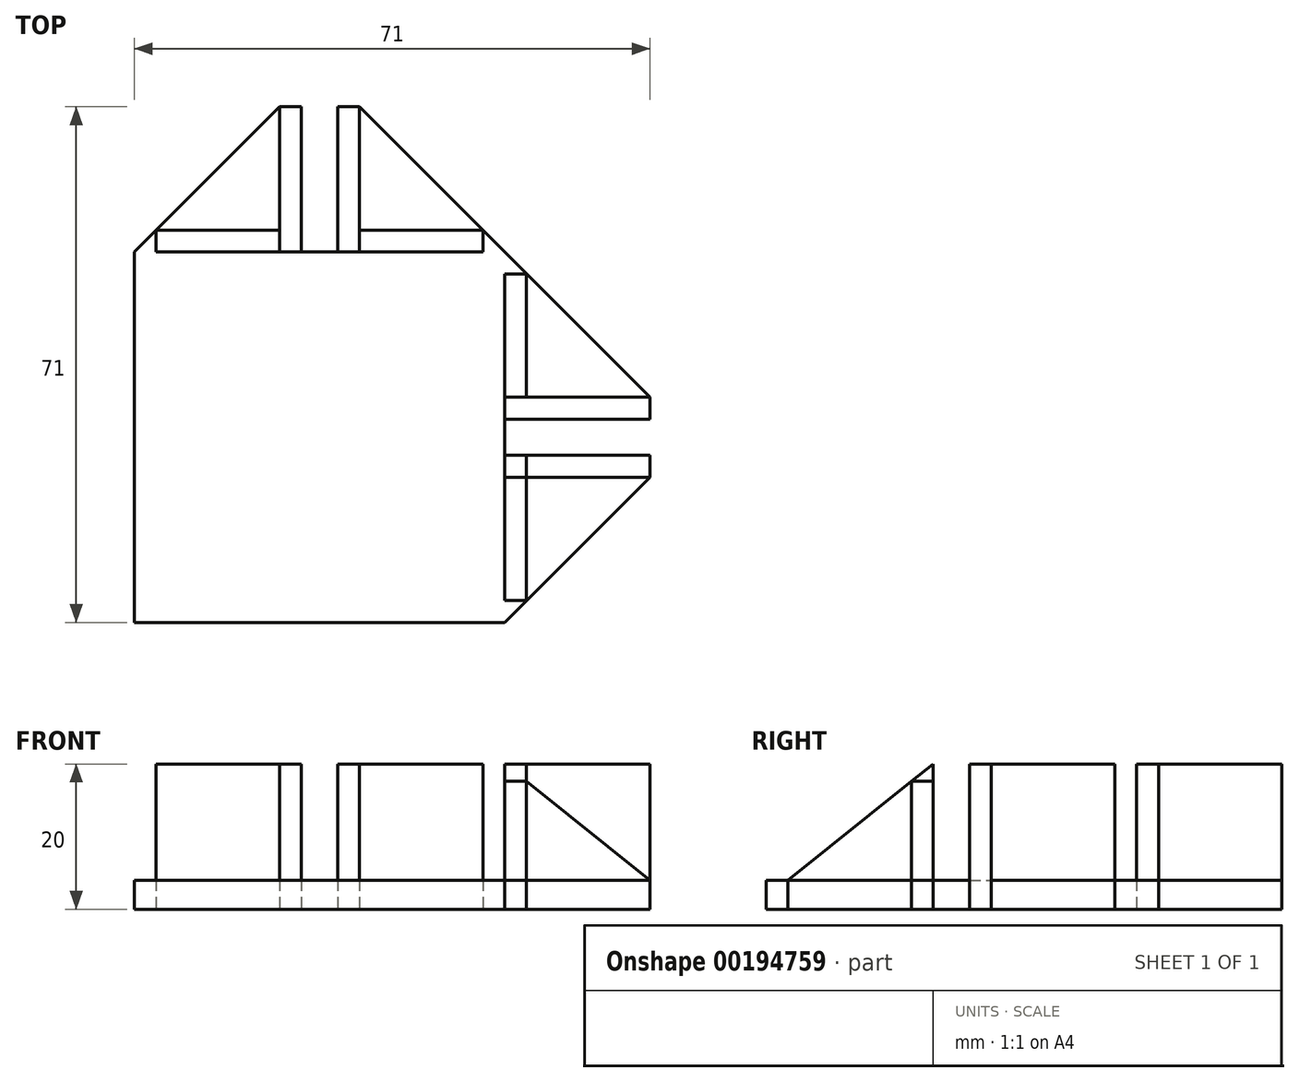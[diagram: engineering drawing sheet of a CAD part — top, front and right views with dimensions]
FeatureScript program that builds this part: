
annotation { "Feature Type Name" : "Feature", "Feature Type Description" : "" }
export const myFeature = defineFeature(function(context is Context, id is Id, definition is map)
    precondition{}
    {
        {
            var Q0;
            Q0=qCreatedBy(makeId("Top.planeOp"),FACE);
            var sketch = newSketch(context, id + "F0", { "sketchPlane" : qUnion([Q0])});
            skLineSegment(sketch, "E0.bottom", {"start": v(25.5, -25.5) * mm, "end": v(-25.5, -25.5) * mm});
            skLineSegment(sketch, "E0.top", {"start": v(25.5, 25.5) * mm, "end": v(-25.5, 25.5) * mm});
            skLineSegment(sketch, "E0.left", {"start": v(25.5, -25.5) * mm, "end": v(25.5, 25.5) * mm});
            skLineSegment(sketch, "E0.right", {"start": v(-25.5, -25.5) * mm, "end": v(-25.5, 25.5) * mm});
            skPoint(sketch, "E0.middle", {"position": v(0, 0) * mm});
            skLineSegment(sketch, "E1", {"start": v(-25.5, 25.5) * mm, "end": v(-5.5, 25.5) * mm});
            skLineSegment(sketch, "E2", {"start": v(-5.5, 25.5) * mm, "end": v(-5.5, 45.5) * mm});
            skLineSegment(sketch, "E3", {"start": v(-5.5, 45.5) * mm, "end": v(-25.5, 25.5) * mm});
            skLineSegment(sketch, "E4.MirrorCS", {"start": v(25.5, 25.5) * mm, "end": v(5.5, 25.5) * mm});
            skLineSegment(sketch, "E5.MirrorCS", {"start": v(5.5, 45.5) * mm, "end": v(25.5, 25.5) * mm});
            skLineSegment(sketch, "E6.MirrorCS", {"start": v(5.5, 25.5) * mm, "end": v(5.5, 45.5) * mm});
            skLineSegment(sketch, "E7", {"start": v(25.5, -25.5) * mm, "end": v(25.5, -5.5) * mm});
            skLineSegment(sketch, "E8", {"start": v(25.5, -5.5) * mm, "end": v(45.5, -5.5) * mm});
            skLineSegment(sketch, "E9", {"start": v(45.5, -5.5) * mm, "end": v(25.5, -25.5) * mm});
            skLineSegment(sketch, "E10.MirrorCS", {"start": v(45.5, 5.5) * mm, "end": v(25.5, 25.5) * mm});
            skLineSegment(sketch, "E11.MirrorCS", {"start": v(25.5, 5.5) * mm, "end": v(45.5, 5.5) * mm});
            skLineSegment(sketch, "E12.MirrorCS", {"start": v(25.5, 25.5) * mm, "end": v(25.5, 5.5) * mm});
            skSolve(sketch);
        }
        {
            var Q0;
            Q0 = qSketchRegion(id + "F0", true);
            extrude(context, id + "F1", {"entities" : qUnion([Q0]), "depth" : 4 * mm});
        }
        {
            var Q0;
            Q0=qCreatedBy(makeId("Top.planeOp"),FACE);
            var sketch = newSketch(context, id + "F2", { "sketchPlane" : qUnion([Q0])});
            skLineSegment(sketch, "E13.0", {"start": v(-5.5, 25.5) * mm, "end": v(-5.5, 45.5) * mm});
            skLineSegment(sketch, "E13.1", {"start": v(5.5, 25.5) * mm, "end": v(-5.5, 25.5) * mm});
            skLineSegment(sketch, "E13.2", {"start": v(5.5, 25.5) * mm, "end": v(5.5, 45.5) * mm});
            skLineSegment(sketch, "E13.3", {"start": v(25.5, 5.5) * mm, "end": v(45.5, 5.5) * mm});
            skLineSegment(sketch, "E13.4", {"start": v(25.5, -5.5) * mm, "end": v(45.5, -5.5) * mm});
            skLineSegment(sketch, "E13.5", {"start": v(25.5, -5.5) * mm, "end": v(25.5, 5.5) * mm});
            skLineSegment(sketch, "E14", {"start": v(-5.5, 45.5) * mm, "end": v(-2.5, 45.5) * mm});
            skLineSegment(sketch, "E15", {"start": v(-2.5, 45.5) * mm, "end": v(-2.5, 25.5) * mm});
            skLineSegment(sketch, "E16.MirrorCS", {"start": v(5.5, 45.5) * mm, "end": v(2.5, 45.5) * mm});
            skLineSegment(sketch, "E17.MirrorCS", {"start": v(2.5, 45.5) * mm, "end": v(2.5, 25.5) * mm});
            skLineSegment(sketch, "E18", {"start": v(45.5, 5.5) * mm, "end": v(45.5, 2.5) * mm});
            skLineSegment(sketch, "E19", {"start": v(45.5, 2.5) * mm, "end": v(25.5, 2.5) * mm});
            skLineSegment(sketch, "E20.MirrorCS", {"start": v(45.5, -2.5) * mm, "end": v(25.5, -2.5) * mm});
            skLineSegment(sketch, "E21.MirrorCS", {"start": v(45.5, -5.5) * mm, "end": v(45.5, -2.5) * mm});
            skLineSegment(sketch, "E22", {"start": v(25.5, -2.5) * mm, "end": v(25.5, -22.5) * mm});
            skLineSegment(sketch, "E23", {"start": v(25.5, -22.5) * mm, "end": v(28.5, -22.5) * mm});
            skLineSegment(sketch, "E24", {"start": v(28.5, -22.5) * mm, "end": v(28.5, -5.5) * mm});
            skLineSegment(sketch, "E25.MirrorCS", {"start": v(25.5, 2.5) * mm, "end": v(25.5, 22.5) * mm});
            skLineSegment(sketch, "E26.MirrorCS", {"start": v(28.5, 22.5) * mm, "end": v(28.5, 5.5) * mm});
            skLineSegment(sketch, "E27.MirrorCS", {"start": v(25.5, 22.5) * mm, "end": v(28.5, 22.5) * mm});
            skLineSegment(sketch, "E28", {"start": v(5.5, 25.5) * mm, "end": v(22.5, 25.5) * mm});
            skLineSegment(sketch, "E29", {"start": v(22.5, 25.5) * mm, "end": v(22.5, 28.5) * mm});
            skLineSegment(sketch, "E30", {"start": v(22.5, 28.5) * mm, "end": v(5.5, 28.5) * mm});
            skLineSegment(sketch, "E31.MirrorCS", {"start": v(-22.5, 28.5) * mm, "end": v(-5.5, 28.5) * mm});
            skLineSegment(sketch, "E32.MirrorCS", {"start": v(-22.5, 25.5) * mm, "end": v(-22.5, 28.5) * mm});
            skLineSegment(sketch, "E33.MirrorCS", {"start": v(-5.5, 25.5) * mm, "end": v(-22.5, 25.5) * mm});
            skSolve(sketch);
        }
        {
            var Q0;
            {var subQ4=sQuery(id+"F2.wireOp",EDGE,"E23");Q0=makeQuery(id+"F2.imprint","IMPRINT",FACE,{"disambiguationData":[TD([[makeQuery(id+"F2.imprint","IMPRINT",EDGE,{"derivedFrom":subQ4}),1.0]])]});}
            var Q1;
            {var subQ3=sQuery(id+"F2.wireOp",EDGE,"E26.MirrorCS");Q1=makeQuery(id+"F2.imprint","IMPRINT",FACE,{"disambiguationData":[TD([[makeQuery(id+"F2.imprint","IMPRINT",EDGE,{"derivedFrom":subQ3}),-1.0]])]});}
            var Q2;
            {var subQ0=sQuery(id+"F2.wireOp",EDGE,"E28");Q2=makeQuery(id+"F2.imprint","IMPRINT",FACE,{"disambiguationData":[TD([[makeQuery(id+"F2.imprint","IMPRINT",EDGE,{"derivedFrom":subQ0}),1.0]])]});}
            var Q3;
            {var subQ2=sQuery(id+"F2.wireOp",EDGE,"E31.MirrorCS");Q3=makeQuery(id+"F2.imprint","IMPRINT",FACE,{"disambiguationData":[TD([[makeQuery(id+"F2.imprint","IMPRINT",EDGE,{"derivedFrom":subQ2}),-1.0]])]});}
            extrude(context, id + "F3", {"entities" : qUnion([Q0, Q1, Q2, Q3]), "depth" : 20 * mm});
        }
        {
            var Q0;
            {var subQ1=sQuery(id+"F2.wireOp",EDGE,"E18");Q0=makeQuery(id+"F2.imprint","IMPRINT",FACE,{"disambiguationData":[TD([[makeQuery(id+"F2.imprint","IMPRINT",EDGE,{"derivedFrom":subQ1}),-1.0]])]});}
            var Q1;
            {var subQ1=sQuery(id+"F2.wireOp",EDGE,"E20.MirrorCS");Q1=makeQuery(id+"F2.imprint","IMPRINT",FACE,{"disambiguationData":[TD([[makeQuery(id+"F2.imprint","IMPRINT",EDGE,{"derivedFrom":subQ1}),1.0]])]});}
            var Q2;
            {var subQ0=sQuery(id+"F2.wireOp",EDGE,"E16.MirrorCS");Q2=makeQuery(id+"F2.imprint","IMPRINT",FACE,{"disambiguationData":[TD([[makeQuery(id+"F2.imprint","IMPRINT",EDGE,{"derivedFrom":subQ0}),1.0]])]});}
            var Q3;
            {var subQ0=sQuery(id+"F2.wireOp",EDGE,"E14");Q3=makeQuery(id+"F2.imprint","IMPRINT",FACE,{"disambiguationData":[TD([[makeQuery(id+"F2.imprint","IMPRINT",EDGE,{"derivedFrom":subQ0}),-1.0]])]});}
            extrude(context, id + "F4", {"entities" : qUnion([Q0, Q1, Q2, Q3]), "depth" : 20 * mm});
        }
        {
            var Q0;
            Q0=makeQuery(id+"F3.opExtrude","SWEPT_FACE",FACE,{"disambiguationData":[OSD([sQuery(id+"F2.wireOp",EDGE,"E22")])]});
            var sketch = newSketch(context, id + "F5", { "sketchPlane" : qUnion([Q0])});
            skLineSegment(sketch, "E34.0", {"start": v(25.5, 4) * mm, "end": v(-25.5, 4) * mm, "construction": true});
            skLineSegment(sketch, "E34.1", {"start": v(22.5, 20) * mm, "end": v(22.5, 0) * mm, "construction": true});
            skLineSegment(sketch, "E34.2", {"start": v(5.5, 20) * mm, "end": v(22.5, 20) * mm, "construction": true});
            skLineSegment(sketch, "E34.3", {"start": v(2.5, 20) * mm, "end": v(5.5, 20) * mm, "construction": true});
            skLineSegment(sketch, "E34.4", {"start": v(2.5, 20) * mm, "end": v(2.5, 0) * mm, "construction": true});
            skLineSegment(sketch, "E35", {"start": v(2.5, 20) * mm, "end": v(22.5, 4) * mm});
            skLineSegment(sketch, "E36", {"start": v(22.5, 4) * mm, "end": v(22.5, 20) * mm});
            skLineSegment(sketch, "E37", {"start": v(22.5, 20) * mm, "end": v(2.5, 20) * mm});
            skSolve(sketch);
        }
        {
            var Q0;
            {var subQ0=sQuery(id+"F5.wireOp",EDGE,"E37");var subQ1=sQuery(id+"F5.wireOp",EDGE,"E35");var subQ2=makeQuery(id+"F5.imprint","INTERSECT",VERTEX,{"derivedFrom":[subQ1,subQ0]});Q0=makeQuery(id+"F5.imprint","IMPRINT",FACE,{"disambiguationData":[TD([[makeQuery(id+"F5.imprint","IMPRINT",EDGE,{"disambiguationData":[TD([[subQ2,-1.0]])],"derivedFrom":subQ1}),1.0]])]});}
            var Q1;
            {var subQ0=sQuery(id+"F5.wireOp",EDGE,"E36");Q1=makeQuery(id+"F5.imprint","IMPRINT",FACE,{"disambiguationData":[TD([[makeQuery(id+"F5.imprint","IMPRINT",EDGE,{"derivedFrom":subQ0}),-1.0]])]});}
            var Q2;
            Q2=makeQuery(id+"F3.opExtrude","SWEPT_FACE",FACE,{"disambiguationData":[OSD([sQuery(id+"F2.wireOp",EDGE,"E24")])]});
            extrude(context, id + "F6", {"entities" : qUnion([Q0, Q1]), "operationType" : NewBodyOperationType.REMOVE, "endBound" : BoundingType.UP_TO_SURFACE, "oppositeDirection" : true, "endBoundEntityFace" : qUnion([Q2]), "depth" : 25 * mm});
        }
        {
            var Q0;
            Q0=makeQuery(id+"F4.opExtrude","SWEPT_FACE",FACE,{"disambiguationData":[OSD([sQuery(id+"F2.wireOp",EDGE,"E13.4")])]});
            var sketch = newSketch(context, id + "F7", { "sketchPlane" : qUnion([Q0])});
            skLineSegment(sketch, "E38.0", {"start": v(25.5, 20) * mm, "end": v(45.5, 20) * mm, "construction": true});
            skLineSegment(sketch, "E38.1", {"start": v(45.5, 20) * mm, "end": v(45.5, 0) * mm, "construction": true});
            skLineSegment(sketch, "E38.2", {"start": v(45.5, 4) * mm, "end": v(25.5, 4) * mm, "construction": true});
            skLineSegment(sketch, "E38.3", {"start": v(25.5, 20) * mm, "end": v(25.5, 0) * mm, "construction": true});
            skLineSegment(sketch, "E39", {"start": v(25.5, 20) * mm, "end": v(45.5, 4) * mm});
            skLineSegment(sketch, "E40", {"start": v(25.5, 4) * mm, "end": v(25.5, 20) * mm});
            skLineSegment(sketch, "E41", {"start": v(25.5, 4) * mm, "end": v(45.5, 4) * mm});
            skSolve(sketch);
        }
        {
            var Q0;
            {var subQ0=sQuery(id+"F7.wireOp",EDGE,"E39");Q0=makeQuery(id+"F7.imprint","IMPRINT",FACE,{"disambiguationData":[TD([[makeQuery(id+"F7.imprint","IMPRINT",EDGE,{"derivedFrom":subQ0}),1.0]])]});}
            var Q1;
            Q1=makeQuery(id+"F4.opExtrude","SWEPT_FACE",FACE,{"disambiguationData":[OSD([sQuery(id+"F2.wireOp",EDGE,"E20.MirrorCS")])]});
            extrude(context, id + "F8", {"entities" : qUnion([Q0]), "operationType" : NewBodyOperationType.REMOVE, "endBound" : BoundingType.UP_TO_SURFACE, "oppositeDirection" : true, "endBoundEntityFace" : qUnion([Q1]), "depth" : 25 * mm});
        }
    });
